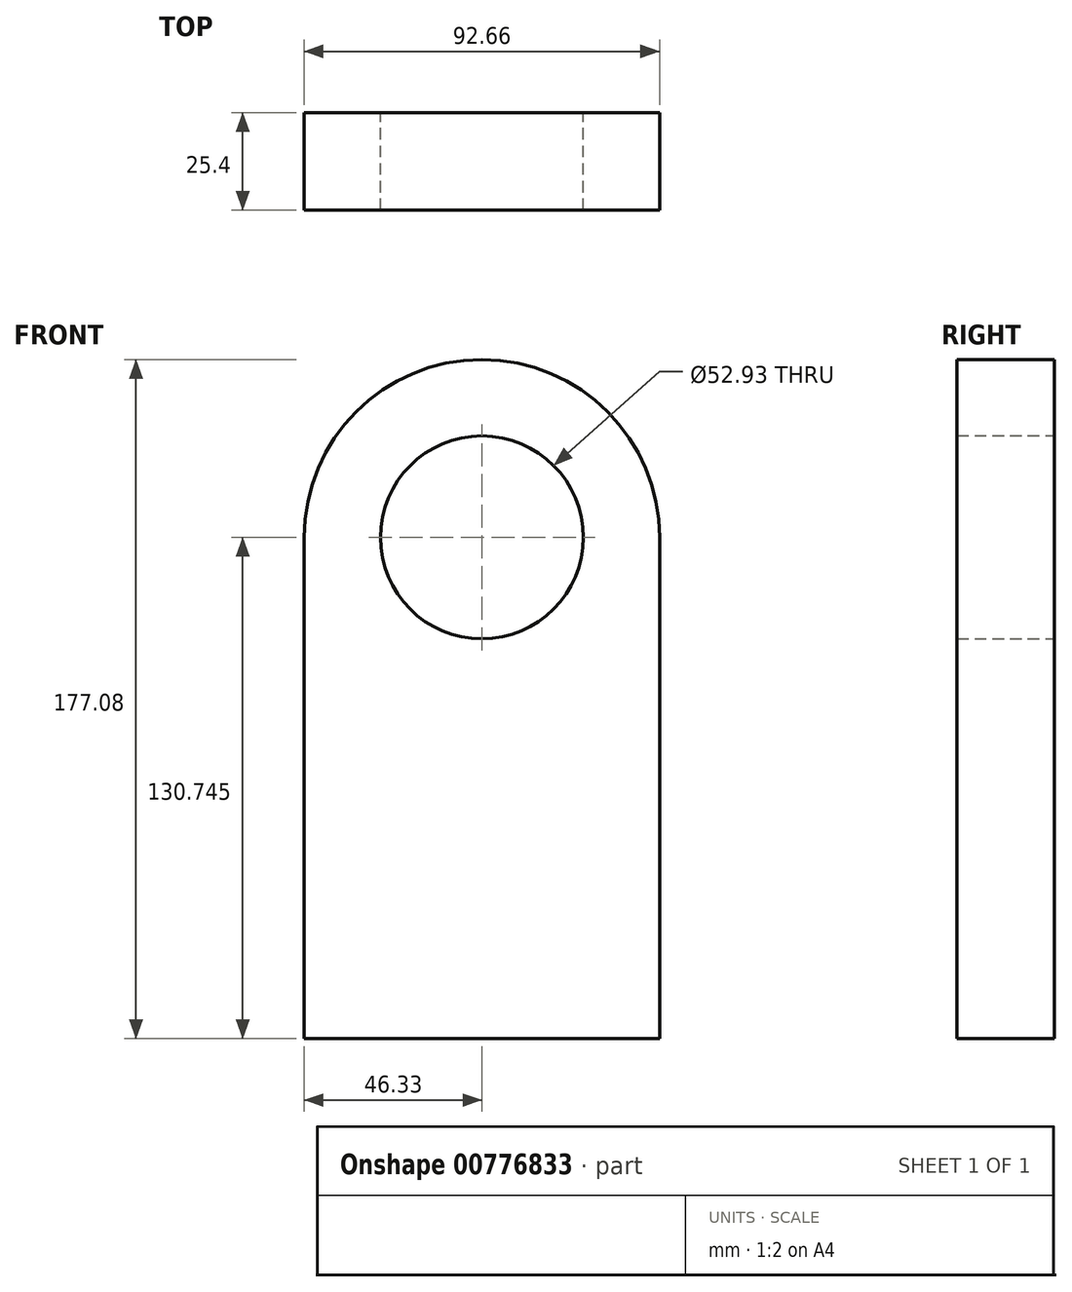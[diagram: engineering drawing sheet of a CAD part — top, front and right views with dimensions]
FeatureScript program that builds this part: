
annotation { "Feature Type Name" : "Feature", "Feature Type Description" : "" }
export const myFeature = defineFeature(function(context is Context, id is Id, definition is map)
    precondition{}
    {
        {
            var Q0;
            Q0=qCreatedBy(makeId("Front.planeOp"),FACE);
            var sketch = newSketch(context, id + "F0", { "sketchPlane" : qUnion([Q0])});
            skLineSegment(sketch, "E0.bottom", {"start": v(-64.1, -73.84) * mm, "end": v(28.57, -73.84) * mm});
            skLineSegment(sketch, "E0.left", {"start": v(-64.1, -73.84) * mm, "end": v(-64.1, 56.9) * mm});
            skLineSegment(sketch, "E0.right", {"start": v(28.57, -73.84) * mm, "end": v(28.57, 56.9) * mm});
            skArc(sketch, "E1", {"start": v(28.57, 56.9) * mm, "mid": v(-17.76, 103.24) * mm, "end": v(-64.1, 56.9) * mm});
            skCircle(sketch, "E2", {"center": v(-17.76, 56.9) * mm, "radius": 26.47 * mm});
            skSolve(sketch);
        }
        {
            var Q0;
            Q0=makeQuery(id+"F0.imprint","IMPRINT",FACE,{"disambiguationData":[TD([[makeQuery(id+"F0.imprint","IMPRINT",EDGE,{"derivedFrom":sQuery(id+"F0.wireOp",EDGE,"E0.bottom")}),1.0]])]});
            extrude(context, id + "F1", {"entities" : qUnion([Q0]), "depth" : 25.4 * mm, "offsetDistance" : 25.4 * mm});
        }
    });
